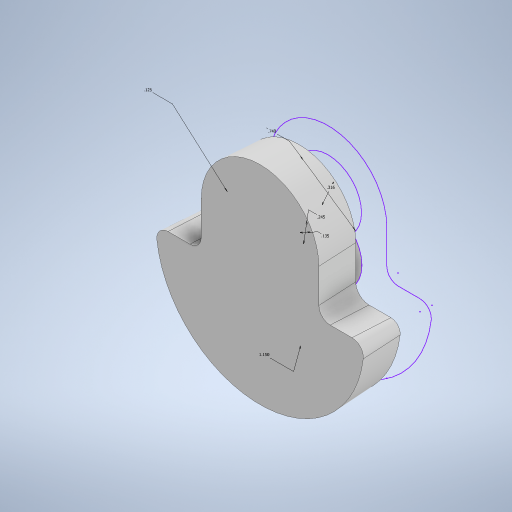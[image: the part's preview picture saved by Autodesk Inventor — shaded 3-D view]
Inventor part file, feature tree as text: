
AUTODESK INVENTOR PART (.ipt)
format: ipt  version: 2023 (Build 270158000, 158)  size: 485,888 bytes
history: native  units: in
note: dims shown in document units (in); Inventor stores cm internally (conversion verified against a paired STEP export)
features: extrude x2, draft x2, sketch x1, fillet x1
ambient origin geometry x8: Origin, YZ Plane, XZ Plane, XY Plane, X Axis, Y Axis, Z Axis, Center Point
bodies: Body1 (feature_tree)
feature tree (6):
  sketch  "Sketch1"  dims[d3=0.866in d15=0.75in d20=0.316in d37=0.75in d44=0.125in d52=0.245in d57=0.74in d58=0.75in d59=0.0in d60=0.32in d61=0.0in d68=0.125in d70=0.135in d71=0.0206in d72=0.0412in d73=1.15in]
  extrude  "Extrusion9"  Depth=0.125in
  extrude  "Extrusion10"  Depth=0.125in
  fillet  "Fillet2"  Radius=0.125in
  draft  "FaceDraft1"
  draft  "FaceDraft2"
